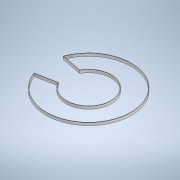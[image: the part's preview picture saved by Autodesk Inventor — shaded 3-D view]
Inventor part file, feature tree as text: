
AUTODESK INVENTOR PART (.ipt)
format: ipt  version: 2021 (Build 250183000, 183)  size: 129,024 bytes
history: native  units: mm
features: extrude x1, sketch x1
ambient origin geometry x8: Origin, YZ Plane, XZ Plane, XY Plane, X Axis, Y Axis, Z Axis, Center Point
bodies: Solid1 (feature_tree)
feature tree (2):
  extrude  "Extrusion1"  Depth=30.0mm TaperAngle=0.0deg
  sketch  "Sketch1"  dims[d0=4.0mm d1=4.0mm d2=4.0mm d3=4.0mm d4=30.0mm d5=0.0mm]
